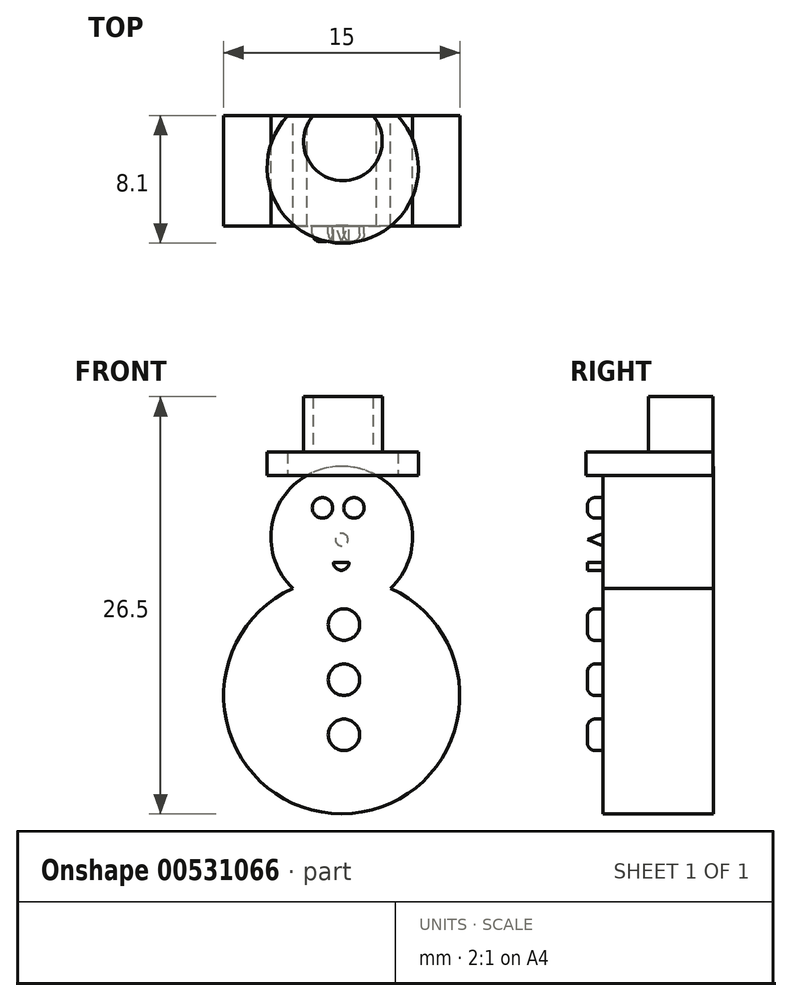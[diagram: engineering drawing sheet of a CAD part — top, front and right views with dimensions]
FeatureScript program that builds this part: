
annotation { "Feature Type Name" : "Feature", "Feature Type Description" : "" }
export const myFeature = defineFeature(function(context is Context, id is Id, definition is map)
    precondition{}
    {
        {
            var Q0;
            Q0=qCreatedBy(makeId("Front.planeOp"),FACE);
            var sketch = newSketch(context, id + "F0", { "sketchPlane" : qUnion([Q0])});
            skCircle(sketch, "E0", {"center": v(0, 0) * mm, "radius": 7.5 * mm});
            skCircle(sketch, "E1", {"center": v(0, 10.08) * mm, "radius": 4.5 * mm});
            skSolve(sketch);
        }
        {
            var Q0;
            {var subQ0=sQuery(id+"F0.wireOp",EDGE,"E1");var subQ1=sQuery(id+"F0.wireOp",EDGE,"E0");var subQ2=makeQuery(id+"F0.imprint","INTERSECT",VERTEX,{"disambiguationData":[OD(0.0)],"derivedFrom":[subQ1,subQ0]});Q0=makeQuery(id+"F0.imprint","IMPRINT",FACE,{"disambiguationData":[TD([[makeQuery(id+"F0.imprint","IMPRINT",EDGE,{"disambiguationData":[TD([[subQ2,1.0]])],"derivedFrom":subQ1}),1.0]])]});}
            var Q1;
            {var subQ0=sQuery(id+"F0.wireOp",EDGE,"E1");var subQ1=sQuery(id+"F0.wireOp",EDGE,"E0");var subQ2=makeQuery(id+"F0.imprint","INTERSECT",VERTEX,{"disambiguationData":[OD(0.0)],"derivedFrom":[subQ1,subQ0]});Q1=makeQuery(id+"F0.imprint","IMPRINT",FACE,{"disambiguationData":[TD([[makeQuery(id+"F0.imprint","IMPRINT",EDGE,{"disambiguationData":[TD([[subQ2,1.0]])],"derivedFrom":subQ1}),-1.0]])]});}
            extrude(context, id + "F1", {"entities" : qUnion([Q0, Q1]), "depth" : 7 * mm, "offsetDistance" : 25 * mm});
        }
        {
            var Q0;
            {var subQ0=sQuery(id+"F0.wireOp",EDGE,"E1");var subQ1=sQuery(id+"F0.wireOp",EDGE,"E0");var subQ2=makeQuery(id+"F0.imprint","INTERSECT",VERTEX,{"disambiguationData":[OD(0.0)],"derivedFrom":[subQ1,subQ0]});Q0=makeQuery(id+"F0.imprint","IMPRINT",FACE,{"disambiguationData":[TD([[makeQuery(id+"F0.imprint","IMPRINT",EDGE,{"disambiguationData":[TD([[subQ2,-1.0]])],"derivedFrom":subQ1}),1.0]])]});}
            extrude(context, id + "F2", {"entities" : qUnion([Q0]), "operationType" : NewBodyOperationType.ADD, "depth" : 7 * mm, "offsetDistance" : 25 * mm});
        }
        {
            var Q0;
            {var subQ0=sQuery(id+"F0.wireOp",EDGE,"E1");Q0=makeQuery(id+"F2.boolean.opBoolean","MERGE",FACE,{"derivedFrom":[makeQuery(id+"F1.opExtrude","CAP_FACE",FACE,{"disambiguationData":[OSD([subQ0])],"isStart":false}),makeQuery(id+"F2.opExtrude","CAP_FACE",FACE,{"disambiguationData":[OSD([sQuery(id+"F0.wireOp",EDGE,"E0"),subQ0])],"isStart":false})]});}
            var sketch = newSketch(context, id + "F3", { "sketchPlane" : qUnion([Q0])});
            skCircle(sketch, "E2", {"center": v(0.14, 1.02) * mm, "radius": 1 * mm});
            skCircle(sketch, "E3", {"center": v(0.14, 4.52) * mm, "radius": 1 * mm});
            skCircle(sketch, "E4", {"center": v(0.14, -2.48) * mm, "radius": 1 * mm});
            skSolve(sketch);
        }
        {
            var Q0;
            Q0=makeQuery(id+"F3.imprint","IMPRINT",FACE,{"disambiguationData":[TD([[makeQuery(id+"F3.imprint","IMPRINT",EDGE,{"derivedFrom":sQuery(id+"F3.wireOp",EDGE,"E3")}),1.0]])]});
            extrude(context, id + "F4", {"entities" : qUnion([Q0]), "operationType" : NewBodyOperationType.ADD, "depth" : 1 * mm, "offsetDistance" : 25 * mm});
        }
        {
            var Q0;
            Q0=makeQuery(id+"F3.imprint","IMPRINT",FACE,{"disambiguationData":[TD([[makeQuery(id+"F3.imprint","IMPRINT",EDGE,{"derivedFrom":sQuery(id+"F3.wireOp",EDGE,"E2")}),1.0]])]});
            var Q1;
            Q1=sQuery(id+"F3.wireOp",EDGE,"E2");
            extrude(context, id + "F5", {"entities" : qUnion([Q0]), "surfaceEntities" : qUnion([Q1]), "depth" : 1 * mm, "offsetDistance" : 25 * mm});
        }
        {
            var Q0;
            Q0=makeQuery(id+"F3.imprint","IMPRINT",FACE,{"disambiguationData":[TD([[makeQuery(id+"F3.imprint","IMPRINT",EDGE,{"derivedFrom":sQuery(id+"F3.wireOp",EDGE,"E4")}),1.0]])]});
            var Q1;
            Q1 = qSketchRegion(id + "F17", true);
            extrude(context, id + "F6", {"entities" : qUnion([Q0, Q1]), "operationType" : NewBodyOperationType.ADD, "depth" : 1 * mm, "offsetDistance" : 25 * mm});
        }
        {
            var Q0;
            {var subQ0=sQuery(id+"F0.wireOp",EDGE,"E1");Q0=makeQuery(id+"F2.boolean.opBoolean","MERGE",FACE,{"derivedFrom":[makeQuery(id+"F1.opExtrude","CAP_FACE",FACE,{"disambiguationData":[OSD([subQ0])],"isStart":false}),makeQuery(id+"F2.opExtrude","CAP_FACE",FACE,{"disambiguationData":[OSD([sQuery(id+"F0.wireOp",EDGE,"E0"),subQ0])],"isStart":false})]});}
            var sketch = newSketch(context, id + "F7", { "sketchPlane" : qUnion([Q0])});
            skCircle(sketch, "E5", {"center": v(-1.22, 11.94) * mm, "radius": 0.65 * mm});
            skCircle(sketch, "E6", {"center": v(0.78, 11.94) * mm, "radius": 0.65 * mm});
            skSolve(sketch);
        }
        {
            var Q0;
            Q0=makeQuery(id+"F7.imprint","IMPRINT",FACE,{"disambiguationData":[TD([[makeQuery(id+"F7.imprint","IMPRINT",EDGE,{"derivedFrom":sQuery(id+"F7.wireOp",EDGE,"E5")}),1.0]])]});
            extrude(context, id + "F8", {"entities" : qUnion([Q0]), "operationType" : NewBodyOperationType.ADD, "depth" : 1 * mm, "offsetDistance" : 25 * mm});
        }
        {
            var Q0;
            Q0=makeQuery(id+"F7.imprint","IMPRINT",FACE,{"disambiguationData":[TD([[makeQuery(id+"F7.imprint","IMPRINT",EDGE,{"derivedFrom":sQuery(id+"F7.wireOp",EDGE,"E6")}),1.0]])]});
            extrude(context, id + "F9", {"entities" : qUnion([Q0]), "operationType" : NewBodyOperationType.ADD, "depth" : 1 * mm, "offsetDistance" : 25 * mm});
        }
        {
            var Q0;
            Q0=qCreatedBy(makeId("Right.planeOp"),FACE);
            var sketch = newSketch(context, id + "F10", { "sketchPlane" : qUnion([Q0])});
            skLineSegment(sketch, "E7", {"start": v(-7, 9.92) * mm, "end": v(-8, 9.92) * mm});
            skLineSegment(sketch, "E8", {"start": v(-8, 9.92) * mm, "end": v(-7, 10.32) * mm});
            skLineSegment(sketch, "E9", {"start": v(-7, 10.32) * mm, "end": v(-7, 9.92) * mm});
            skSolve(sketch);
        }
        {
            var Q0;
            Q0=makeQuery(id+"F10.imprint","IMPRINT",FACE,{"disambiguationData":[TD([[makeQuery(id+"F10.imprint","IMPRINT",EDGE,{"derivedFrom":sQuery(id+"F10.wireOp",EDGE,"E7")}),-1.0]])]});
            var Q1;
            Q1=sQuery(id+"F10.wireOp",EDGE,"E7");
            revolve(context, id + "F11", {"entities" : qUnion([Q0]), "axis" : qUnion([Q1]), "revolveType" : RevolveType.FULL});
        }
        {
            var Q0;
            Q0=qCreatedBy(makeId("Top.planeOp"),FACE);
            cPlane(context, id + "F12", {"entities" : qUnion([Q0]), "cplaneType" : CPlaneType.OFFSET, "offset" : 14 * mm, "width" : 150 * mm, "height" : 150 * mm});
        }
        {
            var Q0;
            Q0=qCreatedBy(id+"F12.planeOp",FACE);
            var sketch = newSketch(context, id + "F13", { "sketchPlane" : qUnion([Q0])});
            skLineSegment(sketch, "E10", {"start": v(-3.44, -0.02) * mm, "end": v(3.56, -0.02) * mm});
            skArc(sketch, "E11", {"start": v(-3.44, -0.02) * mm, "mid": v(0.06, -8.1) * mm, "end": v(3.56, -0.02) * mm});
            skSolve(sketch);
        }
        {
            var Q0;
            Q0=makeQuery(id+"F13.imprint","IMPRINT",FACE,{"disambiguationData":[TD([[makeQuery(id+"F13.imprint","IMPRINT",EDGE,{"derivedFrom":sQuery(id+"F13.wireOp",EDGE,"E10")}),-1.0]])]});
            extrude(context, id + "F14", {"entities" : qUnion([Q0]), "operationType" : NewBodyOperationType.ADD, "depth" : 1.5 * mm, "offsetDistance" : 25 * mm});
        }
        {
            var Q0;
            Q0=makeQuery(id+"F14.opExtrude","CAP_FACE",FACE,{"disambiguationData":[OSD([sQuery(id+"F13.wireOp",EDGE,"E10"),sQuery(id+"F13.wireOp",EDGE,"E11")])],"isStart":false});
            var sketch = newSketch(context, id + "F15", { "sketchPlane" : qUnion([Q0])});
            skLineSegment(sketch, "E12", {"start": v(-1.83, 0) * mm, "end": v(1.97, 0) * mm});
            skArc(sketch, "E13", {"start": v(-1.83, 0) * mm, "mid": v(0.07, -4.13) * mm, "end": v(1.97, 0) * mm});
            skSolve(sketch);
        }
        {
            var Q0;
            {var subQ0=sQuery(id+"F15.wireOp",EDGE,"E13");var subQ1=makeQuery(id+"F14.opExtrude","CAP_EDGE",EDGE,{"disambiguationData":[OSD([sQuery(id+"F13.wireOp",EDGE,"E10")])],"isStart":false});var subQ2=makeQuery(id+"F15.imprint","INTERSECT",VERTEX,{"disambiguationData":[OD(0.0)],"derivedFrom":[subQ1,subQ0]});Q0=makeQuery(id+"F15.imprint","IMPRINT",FACE,{"disambiguationData":[TD([[makeQuery(id+"F15.imprint","IMPRINT",EDGE,{"disambiguationData":[TD([[subQ2,-1.0]])],"derivedFrom":subQ0}),1.0]])]});}
            extrude(context, id + "F16", {"entities" : qUnion([Q0]), "operationType" : NewBodyOperationType.ADD, "depth" : 3.5 * mm, "offsetDistance" : 25 * mm});
        }
        {
            var Q0;
            {var subQ0=sQuery(id+"F0.wireOp",EDGE,"E1");Q0=makeQuery(id+"F2.boolean.opBoolean","MERGE",FACE,{"derivedFrom":[makeQuery(id+"F1.opExtrude","CAP_FACE",FACE,{"disambiguationData":[OSD([subQ0])],"isStart":false}),makeQuery(id+"F2.opExtrude","CAP_FACE",FACE,{"disambiguationData":[OSD([sQuery(id+"F0.wireOp",EDGE,"E0"),subQ0])],"isStart":false})]});}
            var sketch = newSketch(context, id + "F17", { "sketchPlane" : qUnion([Q0])});
            skLineSegment(sketch, "E14", {"start": v(-0.51, 8.47) * mm, "end": v(0.45, 8.47) * mm});
            skArc(sketch, "E15", {"start": v(-0.53, 8.45) * mm, "mid": v(-0.03, 7.97) * mm, "end": v(0.47, 8.45) * mm});
            skPoint(sketch, "E16.visualSharp", {"position": v(-0.53, 8.47) * mm});
            skArc(sketch, "E16.filletArc", {"start": v(-0.51, 8.47) * mm, "mid": v(-0.52, 8.47) * mm, "end": v(-0.53, 8.45) * mm});
            skPoint(sketch, "E17.visualSharp", {"position": v(0.47, 8.47) * mm});
            skArc(sketch, "E17.filletArc", {"start": v(0.47, 8.45) * mm, "mid": v(0.46, 8.47) * mm, "end": v(0.45, 8.47) * mm});
            skSolve(sketch);
        }
        {
            var Q0;
            Q0=makeQuery(id+"F17.imprint","IMPRINT",FACE,{"disambiguationData":[TD([[makeQuery(id+"F17.imprint","IMPRINT",EDGE,{"derivedFrom":sQuery(id+"F17.wireOp",EDGE,"E14")}),-1.0]])]});
            extrude(context, id + "F18", {"entities" : qUnion([Q0]), "operationType" : NewBodyOperationType.ADD, "depth" : 1 * mm, "offsetDistance" : 25 * mm});
        }
        {
            var Q0;
            Q0=makeQuery(id+"F8.opExtrude","CAP_FACE",FACE,{"disambiguationData":[OSD([sQuery(id+"F7.wireOp",EDGE,"E5")])],"isStart":false});
            var Q1;
            Q1=makeQuery(id+"F9.opExtrude","CAP_FACE",FACE,{"disambiguationData":[OSD([sQuery(id+"F7.wireOp",EDGE,"E6")])],"isStart":false});
            var Q2;
            Q2=makeQuery(id+"F4.opExtrude","CAP_FACE",FACE,{"disambiguationData":[OSD([sQuery(id+"F3.wireOp",EDGE,"E3")])],"isStart":false});
            var Q3;
            Q3=makeQuery(id+"F5.opExtrude","CAP_FACE",FACE,{"disambiguationData":[OSD([sQuery(id+"F3.wireOp",EDGE,"E2")])],"isStart":false});
            var Q4;
            Q4=makeQuery(id+"F6.opExtrude","CAP_FACE",FACE,{"disambiguationData":[OSD([sQuery(id+"F3.wireOp",EDGE,"E4")])],"isStart":false});
            fillet(context, id + "F19", {"entities" : qUnion([Q0, Q1, Q2, Q3, Q4]), "radius" : .5 * mm, "tangentPropagation" : true, "allowEdgeOverflow" : false});
        }
    });
